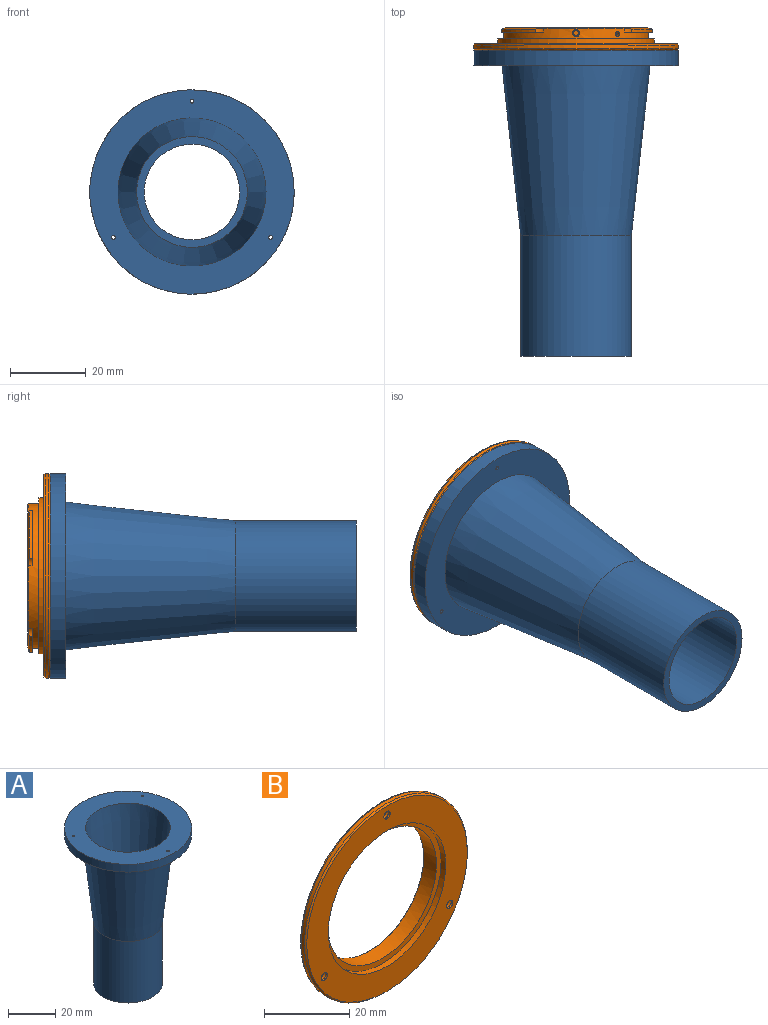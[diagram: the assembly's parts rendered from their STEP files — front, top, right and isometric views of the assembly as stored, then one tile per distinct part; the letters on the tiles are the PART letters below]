
ASSEMBLY  parts=2 mates=1
PART A: 11 faces, bbox 54x54x80.8 mm
  f0: cylinder r=27mm len=54mm, axis (0,0,1), area 678.6mm2, adj f1,f2
  f1: plane 54x54mm, normal (0,0,-1), area 1086mm2, adj f0,f3,f8,f9,f10
  f2: plane 54x54mm, normal (0,0,1), area 1270mm2, adj f0,f4,f8,f9,f10
  f3: cone r=20mm half-angle=6.3deg, axis (0,0,1), area 4840.3mm2, adj f1,f6
  f4: cone r=18mm half-angle=6.3deg, axis (0,0,1), area 4723.5mm2, adj f2,f5
  f5: cylinder r=12.62mm len=32mm, axis (0,0,1), area 2538.4mm2, adj f4,f7
  f6: cylinder r=14.62mm len=32mm, axis (0,0,1), area 2940.5mm2, adj f3,f7
  f7: plane 29.25x29.25mm, normal (0,0,-1), area 171.2mm2, adj f5,f6
  f8: cylinder r=0.5mm len=4mm, axis (0,0,-1), area 12.6mm2, adj f1,f2
  f9: cylinder r=0.5mm len=4mm, axis (0,0,-1), area 12.6mm2, adj f1,f2
  f10: cylinder r=0.5mm len=4mm, axis (0,0,-1), area 12.6mm2, adj f1,f2
PART B: 50 faces, bbox 54x6x54 mm
  f0: bspline ~1.87x1.85mm, area 1.5mm2, adj f2,f11
  f1: cone r=26.99mm half-angle=45deg, axis (0,1,0), area 90.7mm2, adj f8,f33
  f2: cylinder r=0.67mm len=1.33mm, axis (0,0,1), area 4.2mm2, adj f0,f18
  f3: cylinder r=0.67mm len=1.77mm, axis (0.57,0,0.82), area 4.9mm2, adj f11,f18
  f4: cylinder r=19.48mm len=38.95mm, axis (0,-1,0), area 194.3mm2, adj f33,f49
  f5: cylinder r=1.61mm len=3.23mm, axis (0,1,0), area 11.8mm2, adj f19,f25,f26,f27,f48
  f6: cylinder r=1.61mm len=3.23mm, axis (0,1,0), area 11.8mm2, adj f19,f20,f25,f27,f47
  f7: cylinder r=1.61mm len=3.23mm, axis (0,1,0), area 11.8mm2, adj f20,f25,f26,f27,f46
  f8: cylinder r=26.99mm len=53.98mm, axis (0,1,0), area 172.3mm2, adj f1,f34
  f9: cone r=17.96mm half-angle=45deg, axis (0,1,0), area 28.8mm2, adj f18,f32
  f10: cone r=18.52mm half-angle=77.5deg, axis (0,-1,0), area 135.5mm2, adj f11,f22,f24,f31,f32,f35,f36,f37
  f11: cylinder r=19.13mm len=38.27mm, axis (0,1,0), area 269.9mm2, adj f0,f3,f10,f21,f23,f29,f30,f35
  f12: cylinder r=20.63mm len=41.26mm, axis (0,1,0), area 164.6mm2, adj f28,f29
  f13: cylinder r=21.98mm len=43.97mm, axis (0,1,0), area 17.5mm2, adj f27,f28
  f14: cylinder r=26.84mm len=53.68mm, axis (0,1,0), area 66.4mm2, adj f25,f34
  f15: cylinder r=1.05mm len=2.1mm, axis (0,1,0), area 3.4mm2, adj f33,f46
  f16: cylinder r=1.05mm len=2.1mm, axis (0,1,0), area 3.4mm2, adj f33,f47
  f17: cylinder r=1.05mm len=2.1mm, axis (0,1,0), area 3.4mm2, adj f33,f48
  f18: cylinder r=17.96mm len=35.93mm, axis (0,1,0), area 474.8mm2, adj f2,f3,f9,f49
  f19: cylinder r=25.4mm len=43.14mm, axis (0,1,0), area 6.5mm2, adj f5,f6,f25,f27
  f20: cylinder r=25.4mm len=37.36mm, axis (0,1,0), area 6.5mm2, adj f6,f7,f25,f27
  f21: plane 14.5x11.12mm, normal (0,-1,0), area 17.7mm2, adj f11,f22,f36,f39
  f22: cylinder r=20.21mm len=12.53mm, axis (0,1,0), area 12.8mm2, adj f10,f21,f36,f39
  f23: plane 19.42x7.52mm, normal (0,-1,0), area 20.9mm2, adj f11,f24,f37,f40
  f24: cylinder r=20.21mm len=17.42mm, axis (0,1,0), area 15.2mm2, adj f10,f23,f37,f40
  f25: plane 53.68x53.68mm, normal (0,1,0), area 235.8mm2, adj f5,f6,f7,f14,f19,f20,f26
  f26: cylinder r=25.4mm len=37.36mm, axis (0,1,0), area 6.5mm2, adj f5,f7,f25,f27
  f27: plane 50.8x50.79mm, normal (0,1,0), area 480.2mm2, adj f5,f6,f7,f13,f19,f20,f26,f41
  f28: plane 43.97x43.97mm, normal (0,1,0), area 181.1mm2, adj f12,f13
  f29: plane 41.26x41.26mm, normal (0,1,0), area 187.2mm2, adj f11,f12
  f30: plane 18.42x6.32mm, normal (0,-1,0), area 19.2mm2, adj f11,f31,f35,f38
  f31: cylinder r=20.21mm len=16.26mm, axis (0,1,0), area 13.9mm2, adj f10,f30,f35,f38
  f32: plane 37.05x37.05mm, normal (0,1,0), area 43.9mm2, adj f9,f10
  f33: plane 53.21x53.21mm, normal (0,-1,0), area 1022mm2, adj f1,f4,f15,f16,f17
  f34: plane 53.98x53.98mm, normal (0,1,0), area 24.7mm2, adj f8,f14
  f35: cylinder r=2.22mm len=1.99mm, axis (0,1,0), area 2mm2, adj f10,f11,f30,f31
  f36: cylinder r=2.22mm len=1.97mm, axis (0,1,0), area 2mm2, adj f10,f11,f21,f22
  f37: cylinder r=2.22mm len=1.52mm, axis (0,1,0), area 2mm2, adj f10,f11,f23,f24
  f38: cylinder r=2.22mm len=1.5mm, axis (0,1,0), area 2mm2, adj f10,f11,f30,f31
  f39: cylinder r=2.22mm len=2.1mm, axis (0,1,0), area 2mm2, adj f10,f11,f21,f22
  f40: cylinder r=2.22mm len=2.04mm, axis (0,1,0), area 2mm2, adj f10,f11,f23,f24
  f41: plane 1.27x0.75mm, normal (0,0,1), area 1mm2, adj f27,f42,f44,f45
  f42: cylinder r=0.99mm len=1.98mm, axis (0,1,0), area 4mm2, adj f27,f41,f43,f45
  f43: plane 1.27x0.75mm, normal (0,0,-1), area 1mm2, adj f27,f42,f44,f45
  f44: cylinder r=0.99mm len=1.98mm, axis (0,1,0), area 4mm2, adj f27,f41,f43,f45
  f45: plane 2.73x1.98mm, normal (0,1,0), area 4.6mm2, adj f41,f42,f43,f44
  f46: plane 3.23x3.23mm, normal (0,1,0), area 4.7mm2, adj f7,f15
  f47: plane 3.23x3.23mm, normal (0,1,0), area 4.7mm2, adj f6,f16
  f48: plane 3.23x3.23mm, normal (0,1,0), area 4.7mm2, adj f5,f17
  f49: plane 38.95x38.95mm, normal (0,-1,0), area 177.8mm2, adj f4,f18
PLACE A rot(axis=(-1,0,0),90deg) t=(79.32,14.82,27.12)mm
PLACE B t=(79.32,14.82,27.12)mm
MATE fastened A.f10 <-> B.f7  axis (0,1,0) through (79.32,14.82,51.12)mm
